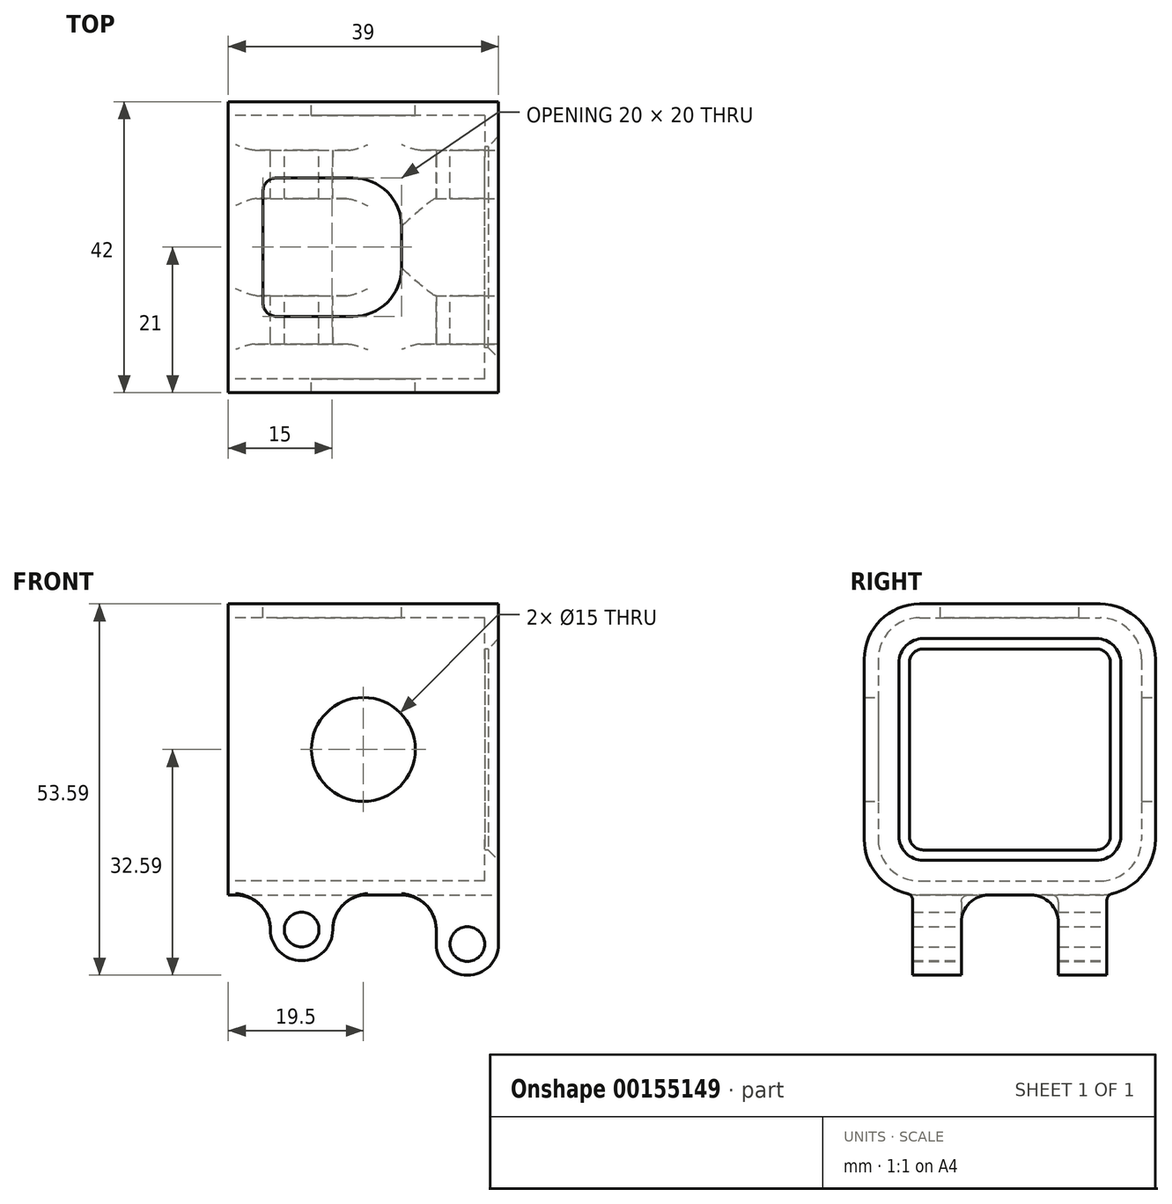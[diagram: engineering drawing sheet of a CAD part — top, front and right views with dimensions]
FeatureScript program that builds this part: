
annotation { "Feature Type Name" : "Feature", "Feature Type Description" : "" }
export const myFeature = defineFeature(function(context is Context, id is Id, definition is map)
    precondition{}
    {
        {
            var Q0;
            Q0=qCreatedBy(makeId("Right.planeOp"),FACE);
            var sketch = newSketch(context, id + "F0", { "sketchPlane" : qUnion([Q0])});
            skLineSegment(sketch, "E0.bottom", {"start": v(-13, 21) * mm, "end": v(13, 21) * mm});
            skLineSegment(sketch, "E0.top", {"start": v(-13, -21) * mm, "end": v(13, -21) * mm});
            skLineSegment(sketch, "E0.left", {"start": v(-21, 13) * mm, "end": v(-21, -13) * mm});
            skLineSegment(sketch, "E0.right", {"start": v(21, 13) * mm, "end": v(21, -13) * mm});
            skLineSegment(sketch, "E1.bottom", {"start": v(-13, 19) * mm, "end": v(13, 19) * mm});
            skLineSegment(sketch, "E1.top", {"start": v(-13, -19) * mm, "end": v(13, -19) * mm});
            skLineSegment(sketch, "E1.left", {"start": v(-19, 13) * mm, "end": v(-19, -13) * mm});
            skLineSegment(sketch, "E1.right", {"start": v(19, 13) * mm, "end": v(19, -13) * mm});
            skPoint(sketch, "E2.visualSharp", {"position": v(-19, 19) * mm});
            skArc(sketch, "E2.filletArc", {"start": v(-13, 19) * mm, "mid": v(-17.24, 17.24) * mm, "end": v(-19, 13) * mm});
            skPoint(sketch, "E3.visualSharp", {"position": v(19, 19) * mm});
            skArc(sketch, "E3.filletArc", {"start": v(19, 13) * mm, "mid": v(17.24, 17.24) * mm, "end": v(13, 19) * mm});
            skPoint(sketch, "E4.visualSharp", {"position": v(19, -19) * mm});
            skArc(sketch, "E4.filletArc", {"start": v(13, -19) * mm, "mid": v(17.24, -17.24) * mm, "end": v(19, -13) * mm});
            skPoint(sketch, "E5.visualSharp", {"position": v(-19, -19) * mm});
            skArc(sketch, "E5.filletArc", {"start": v(-19, -13) * mm, "mid": v(-17.24, -17.24) * mm, "end": v(-13, -19) * mm});
            skPoint(sketch, "E6.visualSharp", {"position": v(-21, -21) * mm});
            skArc(sketch, "E6.filletArc", {"start": v(-21, -13) * mm, "mid": v(-18.66, -18.66) * mm, "end": v(-13, -21) * mm});
            skPoint(sketch, "E7.visualSharp", {"position": v(21, -21) * mm});
            skArc(sketch, "E7.filletArc", {"start": v(13, -21) * mm, "mid": v(18.66, -18.66) * mm, "end": v(21, -13) * mm});
            skPoint(sketch, "E8.visualSharp", {"position": v(21, 21) * mm});
            skArc(sketch, "E8.filletArc", {"start": v(21, 13) * mm, "mid": v(18.66, 18.66) * mm, "end": v(13, 21) * mm});
            skPoint(sketch, "E9.visualSharp", {"position": v(-21, 21) * mm});
            skArc(sketch, "E9.filletArc", {"start": v(-13, 21) * mm, "mid": v(-18.66, 18.66) * mm, "end": v(-21, 13) * mm});
            skSolve(sketch);
        }
        {
            var Q0;
            Q0=qSketchRegion(id+"F0",true);
            extrude(context, id + "F1", {"entities" : qUnion([Q0]), "endBound" : BoundingType.SYMMETRIC, "depth" : 37 * mm});
        }
        {
            var Q0;
            Q0=makeQuery(id+"F1.opExtrude","CAP_FACE",FACE,{"disambiguationData":[OSD([sQuery(id+"F0.wireOp",EDGE,"E0.bottom"),sQuery(id+"F0.wireOp",EDGE,"E0.top"),sQuery(id+"F0.wireOp",EDGE,"E0.left"),sQuery(id+"F0.wireOp",EDGE,"E0.right"),sQuery(id+"F0.wireOp",EDGE,"E1.bottom"),sQuery(id+"F0.wireOp",EDGE,"E1.top"),sQuery(id+"F0.wireOp",EDGE,"E1.left"),sQuery(id+"F0.wireOp",EDGE,"E1.right"),sQuery(id+"F0.wireOp",EDGE,"E2.filletArc"),sQuery(id+"F0.wireOp",EDGE,"E3.filletArc"),sQuery(id+"F0.wireOp",EDGE,"E4.filletArc"),sQuery(id+"F0.wireOp",EDGE,"E5.filletArc"),sQuery(id+"F0.wireOp",EDGE,"E6.filletArc"),sQuery(id+"F0.wireOp",EDGE,"E7.filletArc"),sQuery(id+"F0.wireOp",EDGE,"E8.filletArc"),sQuery(id+"F0.wireOp",EDGE,"E9.filletArc")])],"isStart":false});
            var sketch = newSketch(context, id + "F2", { "sketchPlane" : qUnion([Q0])});
            skLineSegment(sketch, "E10.bottom", {"start": v(-12.5, 14.5) * mm, "end": v(12.5, 14.5) * mm});
            skLineSegment(sketch, "E10.top", {"start": v(-12.5, -14.5) * mm, "end": v(12.5, -14.5) * mm});
            skLineSegment(sketch, "E10.left", {"start": v(-14.5, 12.5) * mm, "end": v(-14.5, -12.5) * mm});
            skLineSegment(sketch, "E10.right", {"start": v(14.5, 12.5) * mm, "end": v(14.5, -12.5) * mm});
            skLineSegment(sketch, "E11.bottom", {"start": v(-13, 21) * mm, "end": v(13, 21) * mm});
            skLineSegment(sketch, "E11.top", {"start": v(-13, -21) * mm, "end": v(13, -21) * mm});
            skLineSegment(sketch, "E11.left", {"start": v(-21, 13) * mm, "end": v(-21, -13) * mm});
            skLineSegment(sketch, "E11.right", {"start": v(21, 13) * mm, "end": v(21, -13) * mm});
            skPoint(sketch, "E12.visualSharp", {"position": v(-21, 21) * mm});
            skArc(sketch, "E12.filletArc", {"start": v(-13, 21) * mm, "mid": v(-18.66, 18.66) * mm, "end": v(-21, 13) * mm});
            skPoint(sketch, "E13.visualSharp", {"position": v(-21, -21) * mm});
            skArc(sketch, "E13.filletArc", {"start": v(-21, -13) * mm, "mid": v(-18.66, -18.66) * mm, "end": v(-13, -21) * mm});
            skPoint(sketch, "E14.visualSharp", {"position": v(21, -21) * mm});
            skArc(sketch, "E14.filletArc", {"start": v(13, -21) * mm, "mid": v(18.66, -18.66) * mm, "end": v(21, -13) * mm});
            skPoint(sketch, "E15.visualSharp", {"position": v(21, 21) * mm});
            skArc(sketch, "E15.filletArc", {"start": v(21, 13) * mm, "mid": v(18.66, 18.66) * mm, "end": v(13, 21) * mm});
            skPoint(sketch, "E16.visualSharp", {"position": v(-14.5, 14.5) * mm});
            skArc(sketch, "E16.filletArc", {"start": v(-12.5, 14.5) * mm, "mid": v(-13.91, 13.91) * mm, "end": v(-14.5, 12.5) * mm});
            skPoint(sketch, "E17.visualSharp", {"position": v(-14.5, -14.5) * mm});
            skArc(sketch, "E17.filletArc", {"start": v(-14.5, -12.5) * mm, "mid": v(-13.91, -13.91) * mm, "end": v(-12.5, -14.5) * mm});
            skPoint(sketch, "E18.visualSharp", {"position": v(14.5, -14.5) * mm});
            skArc(sketch, "E18.filletArc", {"start": v(12.5, -14.5) * mm, "mid": v(13.91, -13.91) * mm, "end": v(14.5, -12.5) * mm});
            skPoint(sketch, "E19.visualSharp", {"position": v(14.5, 14.5) * mm});
            skArc(sketch, "E19.filletArc", {"start": v(14.5, 12.5) * mm, "mid": v(13.91, 13.91) * mm, "end": v(12.5, 14.5) * mm});
            skSolve(sketch);
        }
        {
            var Q0;
            Q0=qSketchRegion(id+"F2",true);
            extrude(context, id + "F3", {"entities" : qUnion([Q0]), "operationType" : NewBodyOperationType.ADD, "depth" : 2 * mm});
        }
        {
            var Q0;
            Q0=makeQuery(id+"F3.opExtrude","CAP_EDGE",EDGE,{"disambiguationData":[OSD([sQuery(id+"F2.wireOp",EDGE,"E10.bottom")])],"isStart":false});
            chamfer(context, id + "F4", {"entities" : qUnion([Q0]), "width" : 1.5 * mm, "tangentPropagation" : true});
        }
        {
            var Q0;
            Q0=makeQuery(id+"F3.boolean.opBoolean","MERGE",FACE,{"derivedFrom":[makeQuery(id+"F1.opExtrude","SWEPT_FACE",FACE,{"disambiguationData":[OSD([sQuery(id+"F0.wireOp",EDGE,"E0.bottom")])]}),makeQuery(id+"F3.opExtrude","SWEPT_FACE",FACE,{"disambiguationData":[OSD([sQuery(id+"F2.wireOp",EDGE,"E11.bottom")])]})]});
            var sketch = newSketch(context, id + "F5", { "sketchPlane" : qUnion([Q0])});
            skLineSegment(sketch, "E20.bottom", {"start": v(-11.5, 10) * mm, "end": v(-0.5, 10) * mm});
            skLineSegment(sketch, "E20.top", {"start": v(-11.5, -10) * mm, "end": v(-0.5, -10) * mm});
            skLineSegment(sketch, "E20.left", {"start": v(-13.5, 8) * mm, "end": v(-13.5, -8) * mm});
            skLineSegment(sketch, "E20.right", {"start": v(6.5, 3) * mm, "end": v(6.5, -3) * mm});
            skPoint(sketch, "E21.visualSharp", {"position": v(-13.5, 10) * mm});
            skArc(sketch, "E21.filletArc", {"start": v(-11.5, 10) * mm, "mid": v(-12.91, 9.41) * mm, "end": v(-13.5, 8) * mm});
            skPoint(sketch, "E22.visualSharp", {"position": v(-13.5, -10) * mm});
            skArc(sketch, "E22.filletArc", {"start": v(-13.5, -8) * mm, "mid": v(-12.91, -9.41) * mm, "end": v(-11.5, -10) * mm});
            skPoint(sketch, "E23.visualSharp", {"position": v(6.5, 10) * mm});
            skArc(sketch, "E23.filletArc", {"start": v(6.5, 3) * mm, "mid": v(4.45, 7.95) * mm, "end": v(-0.5, 10) * mm});
            skPoint(sketch, "E24.visualSharp", {"position": v(6.5, -10) * mm});
            skArc(sketch, "E24.filletArc", {"start": v(-0.5, -10) * mm, "mid": v(4.45, -7.95) * mm, "end": v(6.5, -3) * mm});
            skSolve(sketch);
        }
        {
            var Q0;
            Q0=qSketchRegion(id+"F5",true);
            extrude(context, id + "F6", {"entities" : qUnion([Q0]), "operationType" : NewBodyOperationType.REMOVE, "oppositeDirection" : true, "depth" : 5 * mm});
        }
        {
            var Q0;
            Q0=qCreatedBy(makeId("Front.planeOp"),FACE);
            var sketch = newSketch(context, id + "F7", { "sketchPlane" : qUnion([Q0])});
            skCircle(sketch, "E25", {"center": v(16, -28.1) * mm, "radius": 2.5 * mm});
            skCircle(sketch, "E26", {"center": v(-7.9, -26) * mm, "radius": 2.5 * mm});
            skLineSegment(sketch, "E27", {"start": v(-7.9, -26) * mm, "end": v(16, -28.1) * mm, "construction": true});
            skArc(sketch, "E28", {"start": v(11.5, -28.1) * mm, "mid": v(16, -32.6) * mm, "end": v(20.5, -28.1) * mm});
            skArc(sketch, "E29", {"start": v(-12.4, -26) * mm, "mid": v(-7.9, -30.5) * mm, "end": v(-3.4, -26) * mm});
            skLineSegment(sketch, "E30", {"start": v(20.5, -28.1) * mm, "end": v(20.5, -20) * mm});
            skLineSegment(sketch, "E31", {"start": v(11.5, -28.1) * mm, "end": v(11.5, -20) * mm});
            skLineSegment(sketch, "E32", {"start": v(-3.4, -26) * mm, "end": v(-3.4, -20) * mm});
            skLineSegment(sketch, "E33", {"start": v(-3.4, -20) * mm, "end": v(-12.4, -20) * mm});
            skLineSegment(sketch, "E34", {"start": v(-12.4, -20) * mm, "end": v(-12.4, -26) * mm});
            skLineSegment(sketch, "E35", {"start": v(-3.4, -20) * mm, "end": v(11.5, -20) * mm, "construction": true});
            skLineSegment(sketch, "E36", {"start": v(11.5, -20) * mm, "end": v(20.5, -20) * mm});
            skPoint(sketch, "E36.endSnap0", {"position": v(4.05, -20) * mm});
            skSolve(sketch);
        }
        {
            var Q0;
            Q0=qSketchRegion(id+"F7",true);
            extrude(context, id + "F8", {"entities" : qUnion([Q0]), "operationType" : NewBodyOperationType.ADD, "endBound" : BoundingType.SYMMETRIC, "depth" : 28 * mm});
        }
        {
            var Q0;
            Q0=makeQuery(id+"F8.boolean.opBoolean","INTERSECT",EDGE,{"derivedFrom":[makeQuery(id+"F3.boolean.opBoolean","MERGE",FACE,{"derivedFrom":[makeQuery(id+"F1.opExtrude","SWEPT_FACE",FACE,{"disambiguationData":[OSD([sQuery(id+"F0.wireOp",EDGE,"E0.top")])]}),makeQuery(id+"F3.opExtrude","SWEPT_FACE",FACE,{"disambiguationData":[OSD([sQuery(id+"F2.wireOp",EDGE,"E11.top")])]})]}),makeQuery(id+"F8.opExtrude","SWEPT_FACE",FACE,{"disambiguationData":[OSD([sQuery(id+"F7.wireOp",EDGE,"E34")])]})]});
            var Q1;
            Q1=makeQuery(id+"F8.boolean.opBoolean","INTERSECT",EDGE,{"derivedFrom":[makeQuery(id+"F3.boolean.opBoolean","MERGE",FACE,{"derivedFrom":[makeQuery(id+"F1.opExtrude","SWEPT_FACE",FACE,{"disambiguationData":[OSD([sQuery(id+"F0.wireOp",EDGE,"E0.top")])]}),makeQuery(id+"F3.opExtrude","SWEPT_FACE",FACE,{"disambiguationData":[OSD([sQuery(id+"F2.wireOp",EDGE,"E11.top")])]})]}),makeQuery(id+"F8.opExtrude","SWEPT_FACE",FACE,{"disambiguationData":[OSD([sQuery(id+"F7.wireOp",EDGE,"E32")])]})]});
            var Q2;
            Q2=makeQuery(id+"F8.boolean.opBoolean","INTERSECT",EDGE,{"derivedFrom":[makeQuery(id+"F3.boolean.opBoolean","MERGE",FACE,{"derivedFrom":[makeQuery(id+"F1.opExtrude","SWEPT_FACE",FACE,{"disambiguationData":[OSD([sQuery(id+"F0.wireOp",EDGE,"E0.top")])]}),makeQuery(id+"F3.opExtrude","SWEPT_FACE",FACE,{"disambiguationData":[OSD([sQuery(id+"F2.wireOp",EDGE,"E11.top")])]})]}),makeQuery(id+"F8.opExtrude","SWEPT_FACE",FACE,{"disambiguationData":[OSD([sQuery(id+"F7.wireOp",EDGE,"E31")])]})]});
            fillet(context, id + "F9", {"entities" : qUnion([Q0, Q1, Q2]), "radius" : 5 * mm, "tangentPropagation" : true, "allowEdgeOverflow" : false});
        }
        {
            var Q0;
            Q0=makeQuery(id+"F8.boolean.opBoolean","SPLIT",FACE,{"disambiguationData":[TD([makeQuery(id+"F8.opExtrude","SWEPT_FACE",FACE,{"disambiguationData":[OSD([sQuery(id+"F7.wireOp",EDGE,"E31")])]})])],"derivedFrom":makeQuery(id+"F3.boolean.opBoolean","MERGE",FACE,{"derivedFrom":[makeQuery(id+"F1.opExtrude","SWEPT_FACE",FACE,{"disambiguationData":[OSD([sQuery(id+"F0.wireOp",EDGE,"E0.top")])]}),makeQuery(id+"F3.opExtrude","SWEPT_FACE",FACE,{"disambiguationData":[OSD([sQuery(id+"F2.wireOp",EDGE,"E11.top")])]})]})});
            var sketch = newSketch(context, id + "F10", { "sketchPlane" : qUnion([Q0])});
            skLineSegment(sketch, "E37.bottom", {"start": v(-18.5, 7) * mm, "end": v(20.5, 7) * mm});
            skLineSegment(sketch, "E37.top", {"start": v(-18.5, -7) * mm, "end": v(20.5, -7) * mm});
            skLineSegment(sketch, "E37.left", {"start": v(-18.5, 7) * mm, "end": v(-18.5, -7) * mm});
            skLineSegment(sketch, "E37.right", {"start": v(20.5, 7) * mm, "end": v(20.5, -7) * mm});
            skSolve(sketch);
        }
        {
            var Q0;
            Q0 = qSketchRegion(id + "F10", true);
            extrude(context, id + "F11", {"entities" : qUnion([Q0]), "operationType" : NewBodyOperationType.REMOVE, "depth" : 25 * mm});
        }
        {
            var Q0;
            {var subQ2=sQuery(id+"F10.wireOp",EDGE,"E37.bottom");Q0=makeQuery(id+"F11.boolean.opBoolean","COPY",EDGE,{"disambiguationData":[TD([makeQuery(id+"F8.opExtrude","SWEPT_FACE",FACE,{"disambiguationData":[OSD([sQuery(id+"F7.wireOp",EDGE,"E30")])]})])],"derivedFrom":makeQuery(id+"F11.opExtrude","CAP_EDGE",EDGE,{"disambiguationData":[OSD([subQ2])],"isStart":true})});}
            var Q1;
            {var subQ2=sQuery(id+"F10.wireOp",EDGE,"E37.top");Q1=makeQuery(id+"F11.boolean.opBoolean","COPY",EDGE,{"disambiguationData":[TD([makeQuery(id+"F8.opExtrude","SWEPT_FACE",FACE,{"disambiguationData":[OSD([sQuery(id+"F7.wireOp",EDGE,"E30")])]})])],"derivedFrom":makeQuery(id+"F11.opExtrude","CAP_EDGE",EDGE,{"disambiguationData":[OSD([subQ2])],"isStart":true})});}
            fillet(context, id + "F12", {"entities" : qUnion([Q0, Q1]), "radius" : 4 * mm, "tangentPropagation" : true, "allowEdgeOverflow" : false});
        }
        {
            var Q0;
            Q0=makeQuery(id+"F8.boolean.opBoolean","INTERSECT",EDGE,{"derivedFrom":[makeQuery(id+"F3.boolean.opBoolean","MERGE",FACE,{"derivedFrom":[makeQuery(id+"F1.opExtrude","SWEPT_FACE",FACE,{"disambiguationData":[OSD([sQuery(id+"F0.wireOp",EDGE,"E6.filletArc")])]}),makeQuery(id+"F3.opExtrude","SWEPT_FACE",FACE,{"disambiguationData":[OSD([sQuery(id+"F2.wireOp",EDGE,"E13.filletArc")])]})]}),makeQuery(id+"F8.opExtrude","CAP_FACE",FACE,{"disambiguationData":[OSD([sQuery(id+"F7.wireOp",EDGE,"E25"),sQuery(id+"F7.wireOp",EDGE,"E28"),sQuery(id+"F7.wireOp",EDGE,"E30"),sQuery(id+"F7.wireOp",EDGE,"E31"),sQuery(id+"F7.wireOp",EDGE,"E36")])],"isStart":false})]});
            var Q1;
            Q1=makeQuery(id+"F8.boolean.opBoolean","INTERSECT",EDGE,{"derivedFrom":[makeQuery(id+"F3.boolean.opBoolean","MERGE",FACE,{"derivedFrom":[makeQuery(id+"F1.opExtrude","SWEPT_FACE",FACE,{"disambiguationData":[OSD([sQuery(id+"F0.wireOp",EDGE,"E6.filletArc")])]}),makeQuery(id+"F3.opExtrude","SWEPT_FACE",FACE,{"disambiguationData":[OSD([sQuery(id+"F2.wireOp",EDGE,"E13.filletArc")])]})]}),makeQuery(id+"F8.opExtrude","CAP_FACE",FACE,{"disambiguationData":[OSD([sQuery(id+"F7.wireOp",EDGE,"E26"),sQuery(id+"F7.wireOp",EDGE,"E29"),sQuery(id+"F7.wireOp",EDGE,"E32"),sQuery(id+"F7.wireOp",EDGE,"E33"),sQuery(id+"F7.wireOp",EDGE,"E34")])],"isStart":false})]});
            var Q2;
            Q2=makeQuery(id+"F8.boolean.opBoolean","INTERSECT",EDGE,{"derivedFrom":[makeQuery(id+"F3.boolean.opBoolean","MERGE",FACE,{"derivedFrom":[makeQuery(id+"F1.opExtrude","SWEPT_FACE",FACE,{"disambiguationData":[OSD([sQuery(id+"F0.wireOp",EDGE,"E7.filletArc")])]}),makeQuery(id+"F3.opExtrude","SWEPT_FACE",FACE,{"disambiguationData":[OSD([sQuery(id+"F2.wireOp",EDGE,"E14.filletArc")])]})]}),makeQuery(id+"F8.opExtrude","CAP_FACE",FACE,{"disambiguationData":[OSD([sQuery(id+"F7.wireOp",EDGE,"E26"),sQuery(id+"F7.wireOp",EDGE,"E29"),sQuery(id+"F7.wireOp",EDGE,"E32"),sQuery(id+"F7.wireOp",EDGE,"E33"),sQuery(id+"F7.wireOp",EDGE,"E34")])],"isStart":true})]});
            var Q3;
            Q3=makeQuery(id+"F8.boolean.opBoolean","INTERSECT",EDGE,{"derivedFrom":[makeQuery(id+"F3.boolean.opBoolean","MERGE",FACE,{"derivedFrom":[makeQuery(id+"F1.opExtrude","SWEPT_FACE",FACE,{"disambiguationData":[OSD([sQuery(id+"F0.wireOp",EDGE,"E7.filletArc")])]}),makeQuery(id+"F3.opExtrude","SWEPT_FACE",FACE,{"disambiguationData":[OSD([sQuery(id+"F2.wireOp",EDGE,"E14.filletArc")])]})]}),makeQuery(id+"F8.opExtrude","CAP_FACE",FACE,{"disambiguationData":[OSD([sQuery(id+"F7.wireOp",EDGE,"E25"),sQuery(id+"F7.wireOp",EDGE,"E28"),sQuery(id+"F7.wireOp",EDGE,"E30"),sQuery(id+"F7.wireOp",EDGE,"E31"),sQuery(id+"F7.wireOp",EDGE,"E36")])],"isStart":true})]});
            var Q4;
            {var subQ0=sQuery(id+"F2.wireOp",EDGE,"E11.top");var subQ1=sQuery(id+"F0.wireOp",EDGE,"E0.top");var subQ2=sQuery(id+"F10.wireOp",EDGE,"E37.top");Q4=makeQuery(id+"F11.boolean.opBoolean","COPY",EDGE,{"disambiguationData":[TD([makeQuery(id+"F9.opFillet","BLEND_FACE",FACE,{"disambiguationData":[OSD([subQ1,subQ0,sQuery(id+"F7.wireOp",EDGE,"E32")])]})])],"derivedFrom":makeQuery(id+"F11.opExtrude","CAP_EDGE",EDGE,{"disambiguationData":[OSD([subQ2])],"isStart":true})});}
            var Q5;
            {var subQ0=sQuery(id+"F2.wireOp",EDGE,"E11.top");var subQ1=sQuery(id+"F0.wireOp",EDGE,"E0.top");var subQ2=sQuery(id+"F10.wireOp",EDGE,"E37.bottom");Q5=makeQuery(id+"F11.boolean.opBoolean","COPY",EDGE,{"disambiguationData":[TD([makeQuery(id+"F9.opFillet","BLEND_FACE",FACE,{"disambiguationData":[OSD([subQ1,subQ0,sQuery(id+"F7.wireOp",EDGE,"E32")])]})])],"derivedFrom":makeQuery(id+"F11.opExtrude","CAP_EDGE",EDGE,{"disambiguationData":[OSD([subQ2])],"isStart":true})});}
            fillet(context, id + "F13", {"entities" : qUnion([Q0, Q1, Q2, Q3, Q4, Q5]), "radius" : 1 * mm, "tangentPropagation" : true, "allowEdgeOverflow" : false});
        }
        {
            var Q0;
            Q0=qCreatedBy(makeId("Front.planeOp"),FACE);
            var sketch = newSketch(context, id + "F14", { "sketchPlane" : qUnion([Q0])});
            skCircle(sketch, "E38", {"center": v(1, 0) * mm, "radius": 7.5 * mm});
            skSolve(sketch);
        }
        {
            var Q0;
            Q0 = qSketchRegion(id + "F14", true);
            extrude(context, id + "F15", {"entities" : qUnion([Q0]), "operationType" : NewBodyOperationType.REMOVE, "endBound" : BoundingType.SYMMETRIC, "depth" : 45 * mm});
        }
    });
